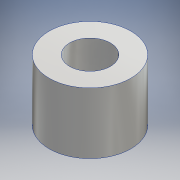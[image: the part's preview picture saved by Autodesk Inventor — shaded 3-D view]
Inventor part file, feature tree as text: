
AUTODESK INVENTOR PART (.ipt)
format: ipt  version: 2016 (Build 200138000, 138)  size: 103,936 bytes
history: native  units: mm
features: other x1, extrude x1, sketch x1
ambient origin geometry x8: Origin, YZ Plane, XZ Plane, XY Plane, X Axis, Y Axis, Z Axis, Center Point
bodies: Body1 (feature_tree)
feature tree (3):
  other  "ソリッド1"
  extrude  "押し出し1"  Depth=4.0mm
  sketch  "スケッチ1"
